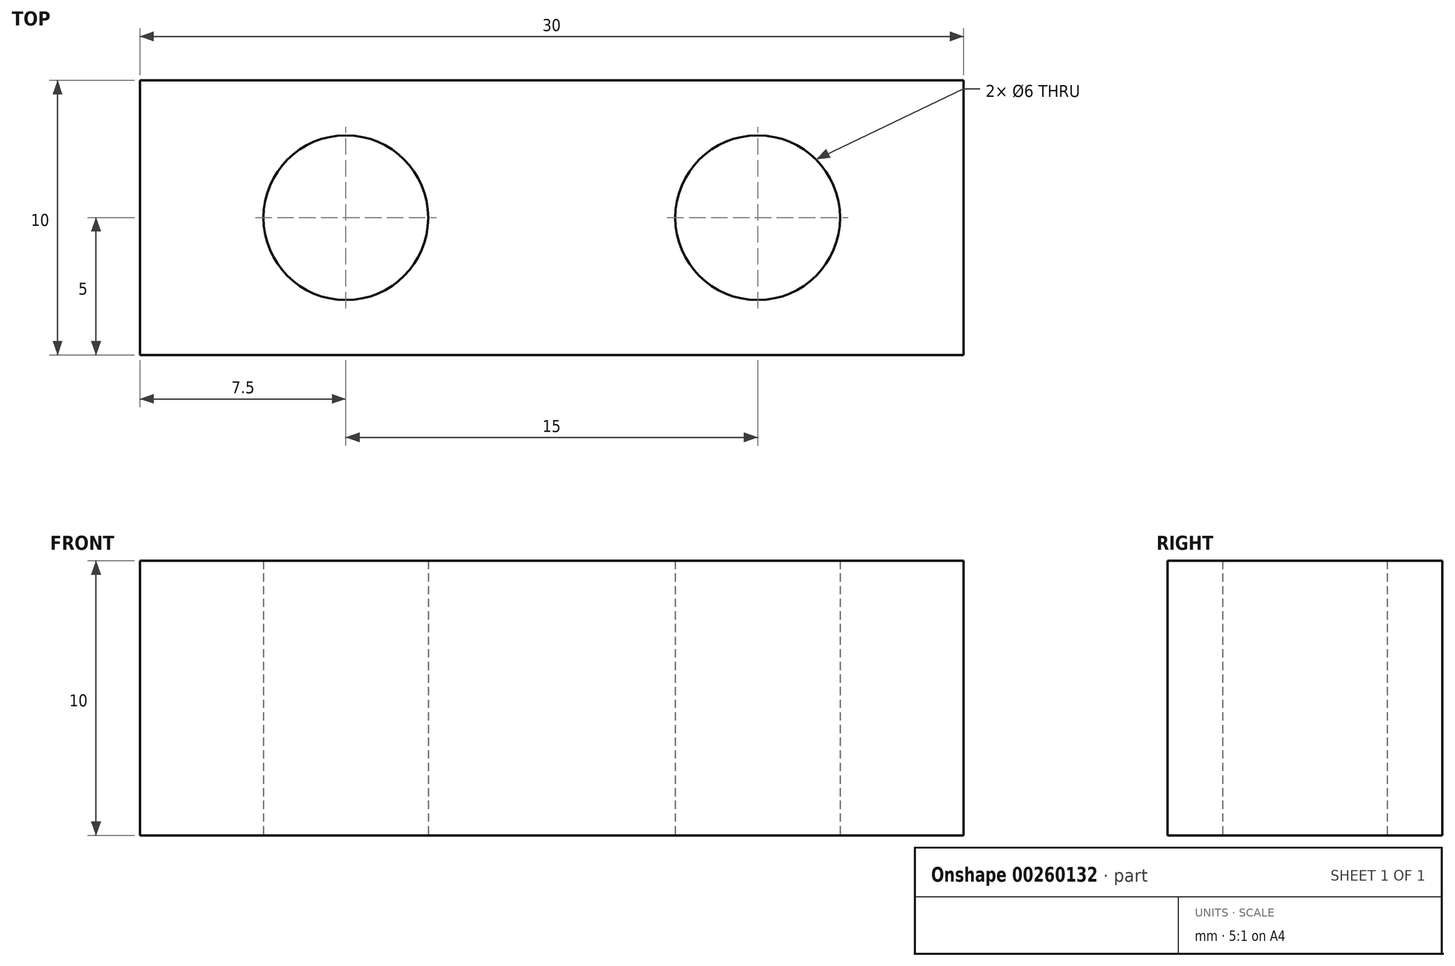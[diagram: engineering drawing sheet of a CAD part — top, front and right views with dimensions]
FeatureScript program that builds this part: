
annotation { "Feature Type Name" : "Feature", "Feature Type Description" : "" }
export const myFeature = defineFeature(function(context is Context, id is Id, definition is map)
    precondition{}
    {
        {
            var Q0;
            Q0=qCreatedBy(makeId("Top.planeOp"),FACE);
            var sketch = newSketch(context, id + "F0", { "sketchPlane" : qUnion([Q0])});
            skLineSegment(sketch, "E0.bottom", {"start": v(15, -5) * mm, "end": v(-15, -5) * mm});
            skLineSegment(sketch, "E0.top", {"start": v(15, 5) * mm, "end": v(-15, 5) * mm});
            skLineSegment(sketch, "E0.left", {"start": v(15, -5) * mm, "end": v(15, 5) * mm});
            skLineSegment(sketch, "E0.right", {"start": v(-15, -5) * mm, "end": v(-15, 5) * mm});
            skPoint(sketch, "E0.middle", {"position": v(0, 0) * mm});
            skLineSegment(sketch, "E1", {"start": v(0, 0) * mm, "end": v(0, 15) * mm, "construction": true});
            skLineSegment(sketch, "E2", {"start": v(0, 15) * mm, "end": v(-7.5, 15) * mm, "construction": true});
            skLineSegment(sketch, "E3", {"start": v(-7.5, 15) * mm, "end": v(-7.5, 0) * mm, "construction": true});
            skCircle(sketch, "E4", {"center": v(-7.5, 0) * mm, "radius": 3 * mm});
            skCircle(sketch, "E5.MirrorC", {"center": v(7.5, 0) * mm, "radius": 3 * mm});
            skSolve(sketch);
        }
        {
            var Q0;
            Q0=makeQuery(id+"F0.imprint","IMPRINT",FACE,{"disambiguationData":[TD([[makeQuery(id+"F0.imprint","IMPRINT",EDGE,{"derivedFrom":sQuery(id+"F0.wireOp",EDGE,"E0.bottom")}),-1.0]])]});
            extrude(context, id + "F1", {"entities" : qUnion([Q0]), "depth" : 10 * mm});
        }
    });
